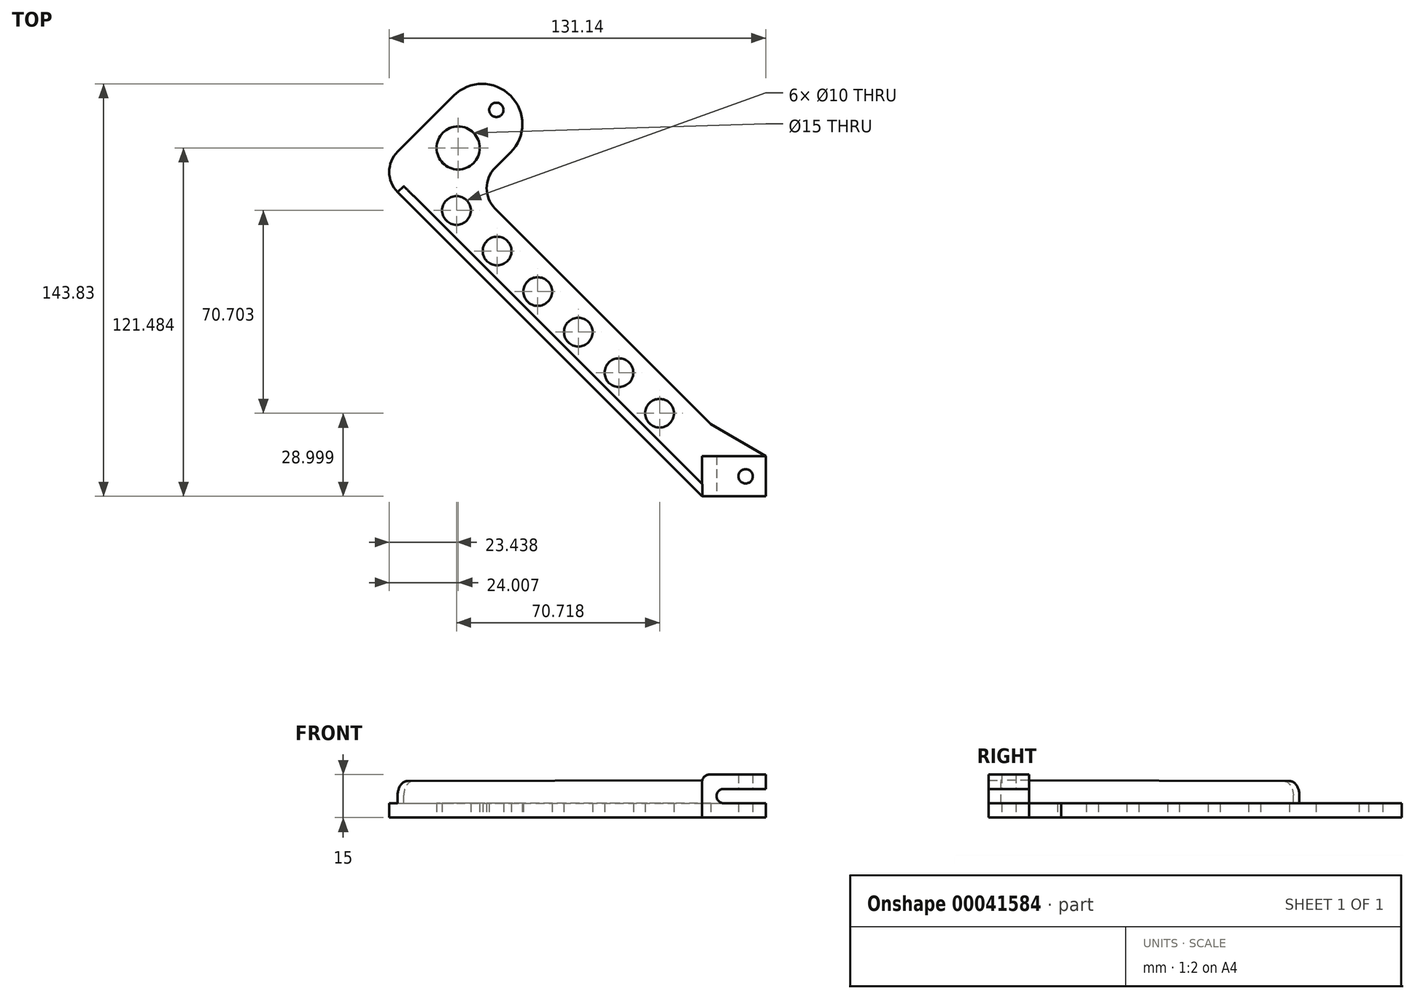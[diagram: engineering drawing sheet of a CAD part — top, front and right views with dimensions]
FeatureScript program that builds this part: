
annotation { "Feature Type Name" : "Feature", "Feature Type Description" : "" }
export const myFeature = defineFeature(function(context is Context, id is Id, definition is map)
    precondition{}
    {
        {
            var Q0;
            Q0=qCreatedBy(makeId("Top.planeOp"),FACE);
            var sketch = newSketch(context, id + "F0", { "sketchPlane" : qUnion([Q0])});
            skLineSegment(sketch, "E0", {"start": v(0, 0) * mm, "end": v(15, 0) * mm, "construction": true});
            skLineSegment(sketch, "E1", {"start": v(0, 0) * mm, "end": v(-113.2, 113.2) * mm, "construction": true});
            skLineSegment(sketch, "E2", {"start": v(0, 0) * mm, "end": v(0, 74.83) * mm, "construction": true});
            skLineSegment(sketch, "E3.0", {"start": v(-4.08, 18.23) * mm, "end": v(-79.27, 93.4) * mm});
            skLineSegment(sketch, "E4.0", {"start": v(-7.14, -7) * mm, "end": v(-113.2, 99.07) * mm});
            skLineSegment(sketch, "E5.0", {"start": v(-7.14, -7) * mm, "end": v(15, -7) * mm});
            skLineSegment(sketch, "E6", {"start": v(15, 7) * mm, "end": v(15, -7) * mm});
            skLineSegment(sketch, "E7", {"start": v(-79.27, 107.55) * mm, "end": v(-73.89, 112.93) * mm});
            skLineSegment(sketch, "E8.0", {"start": v(-113.2, 113.2) * mm, "end": v(-93.69, 132.73) * mm});
            skArc(sketch, "E9", {"start": v(-73.89, 112.93) * mm, "mid": v(-73.89, 132.73) * mm, "end": v(-93.69, 132.73) * mm});
            skLineSegment(sketch, "E10", {"start": v(-73.89, 132.73) * mm, "end": v(-110.38, 96.24) * mm, "construction": true});
            skCircle(sketch, "E11", {"center": v(-78.84, 127.78) * mm, "radius": 2.5 * mm});
            skLineSegment(sketch, "E12", {"start": v(-4.08, 18.23) * mm, "end": v(15, 7) * mm});
            skPoint(sketch, "E13.visualSharp", {"position": v(-86.34, 100.48) * mm});
            skArc(sketch, "E13.filletArc", {"start": v(-79.27, 107.55) * mm, "mid": v(-82.2, 100.48) * mm, "end": v(-79.27, 93.4) * mm});
            skPoint(sketch, "E14.visualSharp", {"position": v(-120.28, 106.14) * mm});
            skArc(sketch, "E14.filletArc", {"start": v(-113.2, 113.2) * mm, "mid": v(-116.14, 106.14) * mm, "end": v(-113.2, 99.07) * mm});
            skCircle(sketch, "E15", {"center": v(-92.13, 114.48) * mm, "radius": 7.5 * mm});
            skCircle(sketch, "E16", {"center": v(-92.7, 92.7) * mm, "radius": 5 * mm});
            skCircle(sketch, "E17.1.0.0", {"center": v(-78.56, 78.56) * mm, "radius": 5 * mm});
            skCircle(sketch, "E17.2.0.0", {"center": v(-64.41, 64.42) * mm, "radius": 5 * mm});
            skCircle(sketch, "E17.3.0.0", {"center": v(-50.27, 50.28) * mm, "radius": 5 * mm});
            skCircle(sketch, "E17.4.0.0", {"center": v(-36.13, 36.14) * mm, "radius": 5 * mm});
            skCircle(sketch, "E17.5.0.0", {"center": v(-21.98, 22) * mm, "radius": 5 * mm});
            skLineSegment(sketch, "E17.direction1", {"start": v(-92.7, 92.7) * mm, "end": v(-78.56, 78.56) * mm, "construction": true});
            skSolve(sketch);
        }
        {
            var Q0;
            Q0=makeQuery(id+"F0.imprint","IMPRINT",FACE,{"disambiguationData":[TD([[makeQuery(id+"F0.imprint","IMPRINT",EDGE,{"derivedFrom":sQuery(id+"F0.wireOp",EDGE,"E3.0")}),1.0]])]});
            extrude(context, id + "F1", {"entities" : qUnion([Q0]), "depth" : 5 * mm});
        }
        {
            var Q0;
            Q0=makeQuery(id+"F1.opExtrude","SWEPT_FACE",FACE,{"disambiguationData":[OSD([sQuery(id+"F0.wireOp",EDGE,"E5.0")])]});
            var sketch = newSketch(context, id + "F2", { "sketchPlane" : qUnion([Q0])});
            skLineSegment(sketch, "E18.bottom", {"start": v(15, 0) * mm, "end": v(-7.14, 0) * mm});
            skLineSegment(sketch, "E18.top", {"start": v(15, 5) * mm, "end": v(0.36, 5) * mm});
            skLineSegment(sketch, "E18.left", {"start": v(15, 0) * mm, "end": v(15, 5) * mm});
            skLineSegment(sketch, "E18.right", {"start": v(-7.14, 0) * mm, "end": v(-7.14, 5) * mm});
            skLineSegment(sketch, "E19", {"start": v(15, 0) * mm, "end": v(15, 15) * mm});
            skLineSegment(sketch, "E20", {"start": v(15, 15) * mm, "end": v(-4.64, 15) * mm});
            skLineSegment(sketch, "E21", {"start": v(-7.14, 12.5) * mm, "end": v(-7.14, 5) * mm});
            skLineSegment(sketch, "E22.0", {"start": v(15, 10) * mm, "end": v(0.36, 10) * mm});
            skLineSegment(sketch, "E23.0", {"start": v(20, 5) * mm, "end": v(-7.14, 5) * mm});
            skLineSegment(sketch, "E24.0", {"start": v(-2.14, 7.5) * mm, "end": v(-2.14, 7.5) * mm});
            skArc(sketch, "E25.filletArc", {"start": v(0.36, 10) * mm, "mid": v(-1.4, 9.27) * mm, "end": v(-2.14, 7.5) * mm});
            skArc(sketch, "E26.filletArc", {"start": v(-2.14, 7.5) * mm, "mid": v(-1.4, 5.73) * mm, "end": v(0.36, 5) * mm});
            skLineSegment(sketch, "E27", {"start": v(15, 10) * mm, "end": v(15, 5) * mm});
            skPoint(sketch, "E28.visualSharp", {"position": v(-7.14, 15) * mm});
            skArc(sketch, "E28.filletArc", {"start": v(-4.64, 15) * mm, "mid": v(-6.4, 14.27) * mm, "end": v(-7.14, 12.5) * mm});
            skPoint(sketch, "E29.newPointB", {"position": v(-7.14, 5) * mm});
            skSolve(sketch);
        }
        {
            var Q0;
            {var subQ5=sQuery(id+"F2.wireOp",EDGE,"E20");Q0=makeQuery(id+"F2.imprint","IMPRINT",FACE,{"disambiguationData":[TD([[makeQuery(id+"F2.imprint","IMPRINT",EDGE,{"derivedFrom":subQ5}),1.0]])]});}
            extrude(context, id + "F3", {"entities" : qUnion([Q0]), "oppositeDirection" : true, "depth" : 14 * mm});
        }
        {
            var Q0;
            Q0=makeQuery(id+"F1.opExtrude","SWEPT_FACE",FACE,{"disambiguationData":[OSD([sQuery(id+"F0.wireOp",EDGE,"E4.0")])]});
            var sketch = newSketch(context, id + "F4", { "sketchPlane" : qUnion([Q0])});
            skLineSegment(sketch, "E30", {"start": v(-0.1, 5) * mm, "end": v(-150.1, 5) * mm});
            skPoint(sketch, "E31.endSnap0", {"position": v(-75.1, 5) * mm});
            skLineSegment(sketch, "E32", {"start": v(-150.1, 0) * mm, "end": v(-150.1, 7.78) * mm});
            skLineSegment(sketch, "E33", {"start": v(-0.1, 0) * mm, "end": v(-150.1, 0) * mm});
            skLineSegment(sketch, "E34", {"start": v(-0.1, 0) * mm, "end": v(-0.1, 13) * mm});
            skLineSegment(sketch, "E35", {"start": v(-145.1, 12.78) * mm, "end": v(-0.1, 13) * mm});
            skPoint(sketch, "E36.visualSharp", {"position": v(-150.1, 12.77) * mm});
            skArc(sketch, "E36.filletArc", {"start": v(-145.1, 12.78) * mm, "mid": v(-148.64, 11.32) * mm, "end": v(-150.1, 7.78) * mm});
            skSolve(sketch);
        }
        {
            var Q0;
            Q0=makeQuery(id+"F1.opExtrude","CAP_FACE",FACE,{"disambiguationData":[OSD([sQuery(id+"F0.wireOp",EDGE,"E3.0"),sQuery(id+"F0.wireOp",EDGE,"E4.0"),sQuery(id+"F0.wireOp",EDGE,"E5.0"),sQuery(id+"F0.wireOp",EDGE,"E6"),sQuery(id+"F0.wireOp",EDGE,"E7"),sQuery(id+"F0.wireOp",EDGE,"E8.0"),sQuery(id+"F0.wireOp",EDGE,"E9"),sQuery(id+"F0.wireOp",EDGE,"E11"),sQuery(id+"F0.wireOp",EDGE,"E12"),sQuery(id+"F0.wireOp",EDGE,"E13.filletArc"),sQuery(id+"F0.wireOp",EDGE,"E14.filletArc"),sQuery(id+"F0.wireOp",EDGE,"E15"),sQuery(id+"F0.wireOp",EDGE,"E16"),sQuery(id+"F0.wireOp",EDGE,"E17.1.0.0"),sQuery(id+"F0.wireOp",EDGE,"E17.2.0.0"),sQuery(id+"F0.wireOp",EDGE,"E17.3.0.0"),sQuery(id+"F0.wireOp",EDGE,"E17.4.0.0"),sQuery(id+"F0.wireOp",EDGE,"E17.5.0.0")])],"isStart":true});
            var sketch = newSketch(context, id + "F5", { "sketchPlane" : qUnion([Q0])});
            skLineSegment(sketch, "E37", {"start": v(15, 0) * mm, "end": v(-14.14, 0) * mm, "construction": true});
            skLineSegment(sketch, "E38", {"start": v(8, -11.12) * mm, "end": v(8, 7) * mm, "construction": true});
            skCircle(sketch, "E39", {"center": v(8, 0) * mm, "radius": 2.5 * mm});
            skSolve(sketch);
        }
        {
            var Q0;
            Q0=makeQuery(id+"F5.imprint","IMPRINT",FACE,{"disambiguationData":[TD([[makeQuery(id+"F5.imprint","IMPRINT",EDGE,{"derivedFrom":sQuery(id+"F5.wireOp",EDGE,"E39")}),1.0]])]});
            extrude(context, id + "F6", {"entities" : qUnion([Q0]), "operationType" : NewBodyOperationType.REMOVE, "oppositeDirection" : true, "depth" : 25 * mm});
        }
        {
            var Q0;
            Q0=makeQuery(id+"F3.opExtrude","SWEPT_FACE",FACE,{"disambiguationData":[OSD([sQuery(id+"F2.wireOp",EDGE,"E20")])]});
            var sketch = newSketch(context, id + "F7", { "sketchPlane" : qUnion([Q0])});
            skLineSegment(sketch, "E40", {"start": v(15, 0) * mm, "end": v(-4.64, 0) * mm, "construction": true});
            skLineSegment(sketch, "E41", {"start": v(8, -7) * mm, "end": v(8, 7) * mm, "construction": true});
            skCircle(sketch, "E42", {"center": v(8, 0) * mm, "radius": 2.5 * mm});
            skSolve(sketch);
        }
        {
            var Q0;
            Q0=makeQuery(id+"F7.imprint","IMPRINT",FACE,{"disambiguationData":[TD([[makeQuery(id+"F7.imprint","IMPRINT",EDGE,{"derivedFrom":sQuery(id+"F7.wireOp",EDGE,"E42")}),1.0]])]});
            extrude(context, id + "F8", {"entities" : qUnion([Q0]), "operationType" : NewBodyOperationType.REMOVE, "oppositeDirection" : true, "depth" : 5 * mm});
        }
        {
            var Q0;
            Q0 = qSketchRegion(id + "F4", true);
            extrude(context, id + "F9", {"entities" : qUnion([Q0]), "operationType" : NewBodyOperationType.ADD, "oppositeDirection" : true, "depth" : 3 * mm});
        }
    });
